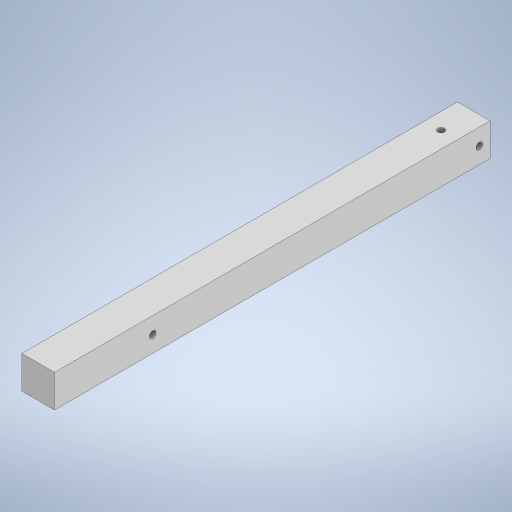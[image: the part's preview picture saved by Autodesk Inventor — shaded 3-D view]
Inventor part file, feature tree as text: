
AUTODESK INVENTOR PART (.ipt)
format: ipt  version: 2023 (Build 270158000, 158)  size: 242,688 bytes
history: native  units: mm
features: sketch x3, hole x2, other x1, extrude x1
ambient origin geometry x8: Origin, YZ Plane, XZ Plane, XY Plane, X Axis, Y Axis, Z Axis, Center Point
bodies: Body1 (feature_tree)
feature tree (7):
  other  "ソリッド1"
  extrude  "押し出し1"  Depth=15.0mm
  hole  "穴1"  [1 undecoded]
  hole  "穴2"  [1 undecoded]
  sketch  "スケッチ1"
  sketch  "スケッチ2"
  sketch  "スケッチ3"
note: 2 required parameter values undecoded (feature->parameter linkage not recoverable at this tier; creation-order binding heuristic only, values carry confidence <= 0.55)
